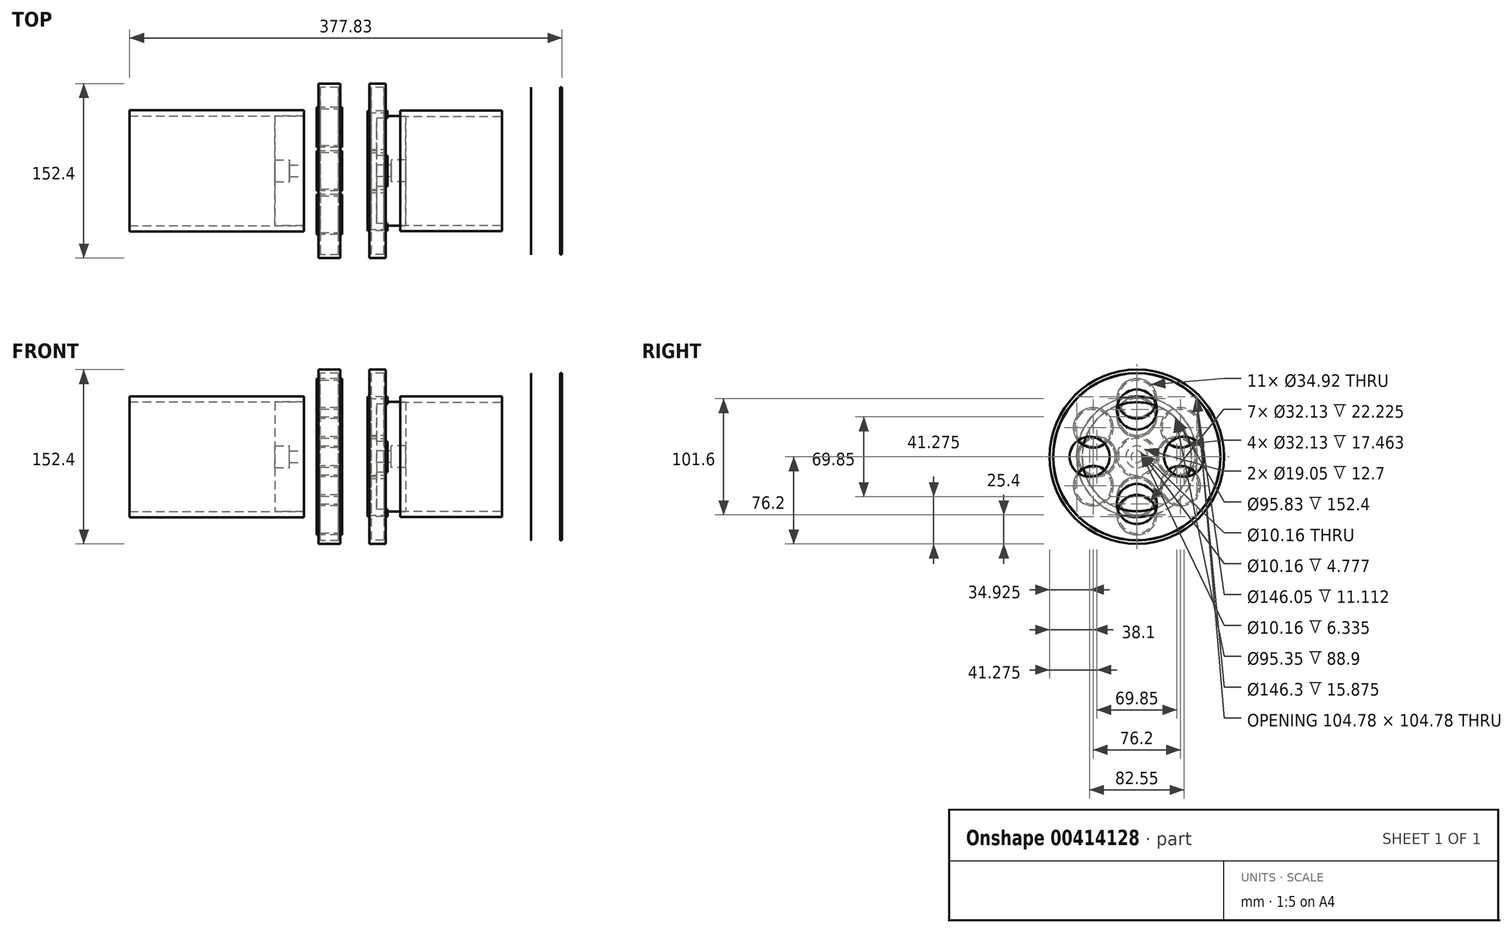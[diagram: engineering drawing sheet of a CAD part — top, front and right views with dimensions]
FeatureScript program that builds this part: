
annotation { "Feature Type Name" : "Feature", "Feature Type Description" : "" }
export const myFeature = defineFeature(function(context is Context, id is Id, definition is map)
    precondition{}
    {
        {
            var Q0;
            Q0=qCreatedBy(makeId("Front.planeOp"),FACE);
            var sketch = newSketch(context, id + "F0", { "sketchPlane" : qUnion([Q0])});
            skLineSegment(sketch, "E0", {"start": v(-64.69, 0) * mm, "end": v(54.13, 0) * mm, "construction": true});
            skLineSegment(sketch, "E1", {"start": v(25.4, 47.92) * mm, "end": v(50.8, 47.92) * mm});
            skLineSegment(sketch, "E2", {"start": v(50.8, 47.92) * mm, "end": v(50.8, 0) * mm});
            skLineSegment(sketch, "E3.trimOffspring", {"start": v(25.4, 0) * mm, "end": v(25.4, 47.92) * mm});
            skLineSegment(sketch, "E4", {"start": v(25.4, 0) * mm, "end": v(50.8, 0) * mm});
            skSolve(sketch);
        }
        {
            var Q0;
            Q0 = qSketchRegion(id + "F0", true);
            var Q1;
            Q1=sQuery(id+"F0.wireOp",EDGE,"E0");
            revolve(context, id + "F1", {"entities" : qUnion([Q0]), "axis" : qUnion([Q1]), "revolveType" : RevolveType.FULL});
        }
        {
            var Q0;
            Q0=makeQuery(id+"F1.opRevolve","SWEPT_FACE",FACE,{"disambiguationData":[OSD([sQuery(id+"F0.wireOp",EDGE,"E2")])]});
            var sketch = newSketch(context, id + "F2", { "sketchPlane" : qUnion([Q0])});
            skCircle(sketch, "E5.0", {"center": v(0, 0) * mm, "radius": 47.92 * mm});
            skCircle(sketch, "E6", {"center": v(0, 0) * mm, "radius": 52.92 * mm});
            skSolve(sketch);
        }
        {
            var Q0;
            Q0 = qSketchRegion(id + "F2", true);
            extrude(context, id + "F3", {"entities" : qUnion([Q0]), "oppositeDirection" : true, "depth" : 152.4 * mm});
        }
        {
            var Q0;
            Q0=makeQuery(id+"F1.opRevolve","SWEPT_FACE",FACE,{"disambiguationData":[OSD([sQuery(id+"F0.wireOp",EDGE,"E2")])]});
            cPlane(context, id + "F4", {"entities" : qUnion([Q0]), "cplaneType" : CPlaneType.OFFSET, "offset" : 12.7 * mm, "width" : 152.4 * mm, "height" : 152.4 * mm});
        }
        {
            var Q0;
            Q0=qCreatedBy(id+"F4.planeOp",FACE);
            var sketch = newSketch(context, id + "F5", { "sketchPlane" : qUnion([Q0])});
            skCircle(sketch, "E7", {"center": v(0, 0) * mm, "radius": 76.2 * mm});
            skLineSegment(sketch, "E8", {"start": v(0, 82.99) * mm, "end": v(0, -50.75) * mm, "construction": true});
            skPoint(sketch, "E8.startSnap0", {"position": v(0, 33.34) * mm});
            skLineSegment(sketch, "E9", {"start": v(-24.05, 0) * mm, "end": v(20.8, 0) * mm, "construction": true});
            skCircle(sketch, "E10", {"center": v(0, 0) * mm, "radius": 17.46 * mm});
            skCircle(sketch, "E11", {"center": v(0, 50.8) * mm, "radius": 17.46 * mm});
            skCircle(sketch, "E12", {"center": v(-38.1, 25.4) * mm, "radius": 17.46 * mm});
            skCircle(sketch, "E13", {"center": v(38.1, 25.4) * mm, "radius": 17.46 * mm});
            skCircle(sketch, "E14.MirrorC", {"center": v(-38.1, -25.4) * mm, "radius": 17.46 * mm});
            skCircle(sketch, "E15.MirrorC", {"center": v(0, -50.8) * mm, "radius": 17.46 * mm});
            skCircle(sketch, "E16.MirrorC", {"center": v(38.1, -25.4) * mm, "radius": 17.46 * mm});
            skSolve(sketch);
        }
        {
            var Q0;
            Q0=makeQuery(id+"F3.opExtrude","CAP_EDGE",EDGE,{"disambiguationData":[OSD([sQuery(id+"F2.wireOp",EDGE,"E6")])],"isStart":true});
            var Q1;
            Q1=sQuery(id+"F5.wireOp",EDGE,"E7");
            loft(context, id + "F6", {"bodyType" : ExtendedToolBodyType.SURFACE, "wireProfilesArray" : [{ "wireProfileEntities" : qUnion([Q0]) }, { "wireProfileEntities" : qUnion([Q1]) }]});
        }
        {
            var Q0;
            Q0=makeQuery(id+"F5.imprint","IMPRINT",FACE,{"disambiguationData":[TD([[makeQuery(id+"F5.imprint","IMPRINT",EDGE,{"derivedFrom":sQuery(id+"F5.wireOp",EDGE,"E7")}),1.0]])]});
            var Q1;
            {var subQ5=sQuery(id+"F5.wireOp",EDGE,"TezqSvzX-SYTh-v60S-WwQ1-Fqk2jw6tep4b");var subQ7=sQuery(id+"F5.wireOp",EDGE,"8UiiZq6U-XtdV-I6FB-cqel-CNXnzfDgyKXF.bottom");var subQ15=makeQuery(id+"F5.imprint","INTERSECT",VERTEX,{"derivedFrom":[subQ5,subQ7]});Q1=makeQuery(id+"F5.imprint","IMPRINT",FACE,{"disambiguationData":[TD([[makeQuery(id+"F5.imprint","IMPRINT",EDGE,{"disambiguationData":[TD([[subQ15,1.0]])],"derivedFrom":subQ5}),-1.0]])]});}
            extrude(context, id + "F7", {"entities" : qUnion([Q0, Q1]), "depth" : 1.59 * mm});
        }
        {
            var Q0;
            Q0=makeQuery(id+"F7.opExtrude","CAP_FACE",FACE,{"disambiguationData":[OSD([sQuery(id+"F5.wireOp",EDGE,"E7"),sQuery(id+"F5.wireOp",EDGE,"TezqSvzX-SYTh-v60S-WwQ1-Fqk2jw6tep4b"),sQuery(id+"F5.wireOp",EDGE,"lQJayD6f-2S0i-9Ahl-4Z4H-LnBthTz2M93B"),sQuery(id+"F5.wireOp",EDGE,"62HEBZpw-P9yn-nqEV-ZTk4-8jesArAcqBT5"),sQuery(id+"F5.wireOp",EDGE,"i2tJHl8b-q1yQ-QXrp-ARdM-XuqOJHXx20dm")])],"isStart":false});
            var sketch = newSketch(context, id + "F8", { "sketchPlane" : qUnion([Q0])});
            skCircle(sketch, "E17.0", {"center": v(0, 0) * mm, "radius": 76.2 * mm});
            skCircle(sketch, "E18", {"center": v(0, 0) * mm, "radius": 73.15 * mm});
            skSolve(sketch);
        }
        {
            var Q0;
            Q0 = qSketchRegion(id + "F8", true);
            extrude(context, id + "F9", {"entities" : qUnion([Q0]), "operationType" : NewBodyOperationType.ADD, "depth" : 17.46 * mm});
        }
        {
            var Q0;
            Q0=makeQuery(id+"F9.opExtrude","CAP_FACE",FACE,{"disambiguationData":[OSD([sQuery(id+"F8.wireOp",EDGE,"E17.0"),sQuery(id+"F8.wireOp",EDGE,"E18")])],"isStart":false});
            var sketch = newSketch(context, id + "F10", { "sketchPlane" : qUnion([Q0])});
            skCircle(sketch, "E19.0", {"center": v(0, 0) * mm, "radius": 73.15 * mm});
            skCircle(sketch, "E20.0", {"center": v(0, 0) * mm, "radius": 17.46 * mm});
            skCircle(sketch, "E21.0", {"center": v(-38.1, 25.4) * mm, "radius": 17.46 * mm});
            skCircle(sketch, "E21.1", {"center": v(0, 50.8) * mm, "radius": 17.46 * mm});
            skCircle(sketch, "E21.2", {"center": v(38.1, 25.4) * mm, "radius": 17.46 * mm});
            skCircle(sketch, "E21.3", {"center": v(38.1, -25.4) * mm, "radius": 17.46 * mm});
            skCircle(sketch, "E21.4", {"center": v(-38.1, -25.4) * mm, "radius": 17.46 * mm});
            skCircle(sketch, "E21.5", {"center": v(0, -50.8) * mm, "radius": 17.46 * mm});
            skSolve(sketch);
        }
        {
            var Q0;
            Q0 = qSketchRegion(id + "F10", true);
            extrude(context, id + "F11", {"entities" : qUnion([Q0]), "operationType" : NewBodyOperationType.ADD, "oppositeDirection" : true, "depth" : 1.59 * mm});
        }
        {
            var Q0;
            Q0=makeQuery(id+"F11.boolean.opBoolean","MERGE",FACE,{"derivedFrom":[makeQuery(id+"F9.opExtrude","CAP_FACE",FACE,{"disambiguationData":[OSD([sQuery(id+"F8.wireOp",EDGE,"E17.0"),sQuery(id+"F8.wireOp",EDGE,"E18")])],"isStart":false}),makeQuery(id+"F11.opExtrude","CAP_FACE",FACE,{"disambiguationData":[OSD([sQuery(id+"F10.wireOp",EDGE,"E19.0"),sQuery(id+"F10.wireOp",EDGE,"688862fc-af98-4b55-a261-9dea444bc1e7.0"),sQuery(id+"F10.wireOp",EDGE,"688862fc-af98-4b55-a261-9dea444bc1e7.1"),sQuery(id+"F10.wireOp",EDGE,"688862fc-af98-4b55-a261-9dea444bc1e7.2"),sQuery(id+"F10.wireOp",EDGE,"688862fc-af98-4b55-a261-9dea444bc1e7.3"),sQuery(id+"F10.wireOp",EDGE,"E20.0")])],"isStart":true})]});
            var sketch = newSketch(context, id + "F12", { "sketchPlane" : qUnion([Q0])});
            skCircle(sketch, "E22.0", {"center": v(0, 0) * mm, "radius": 17.46 * mm});
            skCircle(sketch, "E23", {"center": v(-38.1, 25.4) * mm, "radius": 16.07 * mm});
            skCircle(sketch, "E24", {"center": v(0, 0) * mm, "radius": 16.07 * mm});
            skCircle(sketch, "E25", {"center": v(0, 50.8) * mm, "radius": 16.07 * mm});
            skCircle(sketch, "E26.0", {"center": v(-38.1, 25.4) * mm, "radius": 17.46 * mm});
            skCircle(sketch, "E26.1", {"center": v(0, 50.8) * mm, "radius": 17.46 * mm});
            skCircle(sketch, "E26.2", {"center": v(38.1, 25.4) * mm, "radius": 17.46 * mm});
            skCircle(sketch, "E26.3", {"center": v(38.1, -25.4) * mm, "radius": 17.46 * mm});
            skCircle(sketch, "E26.4", {"center": v(0, -50.8) * mm, "radius": 17.46 * mm});
            skCircle(sketch, "E26.5", {"center": v(-38.1, -25.4) * mm, "radius": 17.46 * mm});
            skCircle(sketch, "E27", {"center": v(-38.1, -25.4) * mm, "radius": 16.07 * mm});
            skCircle(sketch, "E28", {"center": v(0, -50.8) * mm, "radius": 16.07 * mm});
            skCircle(sketch, "E29", {"center": v(38.1, -25.4) * mm, "radius": 16.07 * mm});
            skCircle(sketch, "E30", {"center": v(38.1, 25.4) * mm, "radius": 16.07 * mm});
            skSolve(sketch);
        }
        {
            var Q0;
            Q0 = qSketchRegion(id + "F12", true);
            extrude(context, id + "F13", {"entities" : qUnion([Q0]), "operationType" : NewBodyOperationType.ADD, "depth" : 1.59 * mm, "hasSecondDirection" : true, "secondDirectionOppositeDirection" : true, "secondDirectionDepth" : 20.64 * mm});
        }
        {
            var Q0;
            Q0=makeQuery(id+"F1.opRevolve","SWEPT_FACE",FACE,{"disambiguationData":[OSD([sQuery(id+"F0.wireOp",EDGE,"E3.trimOffspring")])]});
            var sketch = newSketch(context, id + "F14", { "sketchPlane" : qUnion([Q0])});
            skPoint(sketch, "E31", {"position": v(0, 0) * mm});
            skSolve(sketch);
        }
        {
            var Q0;
            Q0=sQuery(id+"F14.wireOp",VERTEX,"E31");
            var Q1;
            Q1=makeQuery(id+"F1.opRevolve","SWEPT_BODY",BODY,{"disambiguationData":[OSD([sQuery(id+"F0.wireOp",EDGE,"E1"),sQuery(id+"F0.wireOp",EDGE,"E2"),sQuery(id+"F0.wireOp",EDGE,"E3.trimOffspring"),sQuery(id+"F0.wireOp",EDGE,"E4")])]});
            hole(context, id + "F15", {"style" : HoleStyle.C_BORE, "endStyle" : HoleEndStyle.THROUGH, "holeDiameter" : 10.16 * mm, "cBoreDiameter" : 19.05 * mm, "cBoreDepth" : 12.7 * mm, "isTappedThrough" : true, "tappedDepth" : 12.7 * mm, "tapClearance" : 3, "locations" : qUnion([Q0]), "scope" : qUnion([Q1]), "startStyle" : HoleStartStyle.PART});
        }
        {
            var Q0;
            Q0=makeQuery(id+"F11.boolean.opBoolean","MERGE",FACE,{"derivedFrom":[makeQuery(id+"F9.opExtrude","CAP_FACE",FACE,{"disambiguationData":[OSD([sQuery(id+"F8.wireOp",EDGE,"E17.0"),sQuery(id+"F8.wireOp",EDGE,"E18")])],"isStart":false}),makeQuery(id+"F11.opExtrude","CAP_FACE",FACE,{"disambiguationData":[OSD([sQuery(id+"F10.wireOp",EDGE,"E19.0"),sQuery(id+"F10.wireOp",EDGE,"688862fc-af98-4b55-a261-9dea444bc1e7.0"),sQuery(id+"F10.wireOp",EDGE,"E20.0"),sQuery(id+"F10.wireOp",EDGE,"38044c42-0bda-4c24-9e16-b2cf3865c2e5.0"),sQuery(id+"F10.wireOp",EDGE,"38044c42-0bda-4c24-9e16-b2cf3865c2e5.1"),sQuery(id+"F10.wireOp",EDGE,"38044c42-0bda-4c24-9e16-b2cf3865c2e5.2"),sQuery(id+"F10.wireOp",EDGE,"38044c42-0bda-4c24-9e16-b2cf3865c2e5.3")])],"isStart":true})]});
            cPlane(context, id + "F16", {"entities" : qUnion([Q0]), "cplaneType" : CPlaneType.OFFSET, "offset" : 0.38 / 50.8 * mm, "width" : 152.4 * mm, "height" : 152.4 * mm});
        }
        {
            var Q0;
            Q0=makeQuery(id+"F6.opLoft","SWEPT_BODY",BODY,{"disambiguationData":[OSD([sQuery(id+"F2.wireOp",EDGE,"E6"),sQuery(id+"F5.wireOp",EDGE,"E7")])]});
            var Q1;
            Q1=makeQuery(id+"F1.opRevolve","SWEPT_BODY",BODY,{"disambiguationData":[OSD([sQuery(id+"F0.wireOp",EDGE,"E1"),sQuery(id+"F0.wireOp",EDGE,"E2"),sQuery(id+"F0.wireOp",EDGE,"7OPXWdJn-CDmA-Pngj-WDx1-qVM9FC09NOPd"),sQuery(id+"F0.wireOp",EDGE,"g0mtmRdn-CkNj-VwcP-hl4j-8XaxVRBAAcs2"),sQuery(id+"F0.wireOp",EDGE,"wG1DruvX-F1o3-LSDn-r3vX-2a799C9GLC4u"),sQuery(id+"F0.wireOp",EDGE,"jPwcn6bF-IbMm-58uC-mqah-eV2g20HCQfEf"),sQuery(id+"F0.wireOp",EDGE,"t1iSLtYn-DT6b-T7c2-KFmK-r26NDrkw72ja"),sQuery(id+"F0.wireOp",EDGE,"E3.trimOffspring")])]});
            var Q2;
            Q2=qCreatedBy(id+"F16.planeOp",FACE);
            mirror(context, id + "F17", {"entities" : qUnion([Q0, Q1]), "mirrorPlane" : qUnion([Q2])});
        }
        {
            var Q0;
            Q0=qCreatedBy(makeId("Front.planeOp"),FACE);
            var sketch = newSketch(context, id + "F18", { "sketchPlane" : qUnion([Q0])});
            skLineSegment(sketch, "E32", {"start": v(0, 0) * mm, "end": v(394.2, 0) * mm, "construction": true});
            skLineSegment(sketch, "E33", {"start": v(107.95, 0) * mm, "end": v(107.95, 76.2) * mm});
            skLineSegment(sketch, "E34", {"start": v(107.95, 76.2) * mm, "end": v(122.24, 76.2) * mm});
            skLineSegment(sketch, "E35", {"start": v(122.24, 76.2) * mm, "end": v(122.24, 0) * mm});
            skLineSegment(sketch, "E36", {"start": v(109.54, 0) * mm, "end": v(109.54, 73.03) * mm});
            skLineSegment(sketch, "E37", {"start": v(109.54, 73.03) * mm, "end": v(120.65, 73.03) * mm});
            skLineSegment(sketch, "E38", {"start": v(120.65, 73.03) * mm, "end": v(120.65, 0) * mm});
            skLineSegment(sketch, "E39", {"start": v(107.95, 0) * mm, "end": v(109.54, 0) * mm});
            skLineSegment(sketch, "E40", {"start": v(120.65, 0) * mm, "end": v(122.24, 0) * mm});
            skSolve(sketch);
        }
        {
            var Q0;
            Q0 = qSketchRegion(id + "F18", true);
            var Q1;
            Q1=sQuery(id+"F18.wireOp",EDGE,"E32");
            revolve(context, id + "F19", {"entities" : qUnion([Q0]), "axis" : qUnion([Q1]), "revolveType" : RevolveType.FULL});
        }
        {
            var Q0;
            Q0=makeQuery(id+"F19.opRevolve","SWEPT_FACE",FACE,{"disambiguationData":[OSD([sQuery(id+"F18.wireOp",EDGE,"E35")])]});
            var sketch = newSketch(context, id + "F20", { "sketchPlane" : qUnion([Q0])});
            skCircle(sketch, "E41", {"center": v(-34.93, 0) * mm, "radius": 17.46 * mm});
            skCircle(sketch, "E42", {"center": v(34.93, 0) * mm, "radius": 17.46 * mm});
            skCircle(sketch, "E43", {"center": v(0, 34.93) * mm, "radius": 17.46 * mm});
            skCircle(sketch, "E44", {"center": v(0, -34.93) * mm, "radius": 17.46 * mm});
            skCircle(sketch, "E45", {"center": v(0, 34.93) * mm, "radius": 16.07 * mm});
            skCircle(sketch, "E46", {"center": v(34.93, 0) * mm, "radius": 16.07 * mm});
            skCircle(sketch, "E47", {"center": v(0, -34.93) * mm, "radius": 16.07 * mm});
            skCircle(sketch, "E48", {"center": v(-34.93, 0) * mm, "radius": 16.07 * mm});
            skSolve(sketch);
        }
        {
            var Q0;
            Q0=makeQuery(id+"F20.imprint","IMPRINT",FACE,{"disambiguationData":[TD([[makeQuery(id+"F20.imprint","IMPRINT",EDGE,{"derivedFrom":sQuery(id+"F20.wireOp",EDGE,"E45")}),1.0]])]});
            var Q1;
            Q1=makeQuery(id+"F20.imprint","IMPRINT",FACE,{"disambiguationData":[TD([[makeQuery(id+"F20.imprint","IMPRINT",EDGE,{"derivedFrom":sQuery(id+"F20.wireOp",EDGE,"E48")}),1.0]])]});
            var Q2;
            Q2=makeQuery(id+"F20.imprint","IMPRINT",FACE,{"disambiguationData":[TD([[makeQuery(id+"F20.imprint","IMPRINT",EDGE,{"derivedFrom":sQuery(id+"F20.wireOp",EDGE,"E47")}),1.0]])]});
            var Q3;
            Q3=makeQuery(id+"F20.imprint","IMPRINT",FACE,{"disambiguationData":[TD([[makeQuery(id+"F20.imprint","IMPRINT",EDGE,{"derivedFrom":sQuery(id+"F20.wireOp",EDGE,"E46")}),1.0]])]});
            var Q4;
            Q4=makeQuery(id+"F19.opRevolve","SWEPT_FACE",FACE,{"disambiguationData":[OSD([sQuery(id+"F18.wireOp",EDGE,"E33")])]});
            extrude(context, id + "F21", {"entities" : qUnion([Q0, Q1, Q2, Q3]), "operationType" : NewBodyOperationType.REMOVE, "endBound" : BoundingType.UP_TO_SURFACE, "oppositeDirection" : true, "endBoundEntityFace" : qUnion([Q4]), "depth" : 25.4 * mm});
        }
        {
            var Q0;
            Q0=makeQuery(id+"F20.imprint","IMPRINT",FACE,{"disambiguationData":[TD([[makeQuery(id+"F20.imprint","IMPRINT",EDGE,{"derivedFrom":sQuery(id+"F20.wireOp",EDGE,"E43")}),1.0]])]});
            var Q1;
            Q1=makeQuery(id+"F20.imprint","IMPRINT",FACE,{"disambiguationData":[TD([[makeQuery(id+"F20.imprint","IMPRINT",EDGE,{"derivedFrom":sQuery(id+"F20.wireOp",EDGE,"E42")}),1.0]])]});
            var Q2;
            Q2=makeQuery(id+"F20.imprint","IMPRINT",FACE,{"disambiguationData":[TD([[makeQuery(id+"F20.imprint","IMPRINT",EDGE,{"derivedFrom":sQuery(id+"F20.wireOp",EDGE,"E44")}),1.0]])]});
            var Q3;
            Q3=makeQuery(id+"F20.imprint","IMPRINT",FACE,{"disambiguationData":[TD([[makeQuery(id+"F20.imprint","IMPRINT",EDGE,{"derivedFrom":sQuery(id+"F20.wireOp",EDGE,"E41")}),1.0]])]});
            extrude(context, id + "F22", {"entities" : qUnion([Q0, Q1, Q2, Q3]), "operationType" : NewBodyOperationType.ADD, "depth" : 1.59 * mm, "hasSecondDirection" : true, "secondDirectionOppositeDirection" : true, "secondDirectionDepth" : 15.88 * mm});
        }
        {
            var Q0;
            Q0=qCreatedBy(makeId("Front.planeOp"),FACE);
            var sketch = newSketch(context, id + "F23", { "sketchPlane" : qUnion([Q0])});
            skLineSegment(sketch, "E49", {"start": v(133.19, 0) * mm, "end": v(56.92, 0) * mm, "construction": true});
            skLineSegment(sketch, "E50.bottom", {"start": v(134.94, 52.65) * mm, "end": v(223.84, 52.65) * mm});
            skLineSegment(sketch, "E50.top", {"start": v(134.94, 47.68) * mm, "end": v(223.84, 47.68) * mm});
            skLineSegment(sketch, "E50.left", {"start": v(134.94, 52.65) * mm, "end": v(134.94, 47.68) * mm});
            skLineSegment(sketch, "E50.right", {"start": v(223.84, 52.65) * mm, "end": v(223.84, 47.68) * mm});
            skSolve(sketch);
        }
        {
            var Q0;
            Q0=makeQuery(id+"F23.imprint","IMPRINT",FACE,{"disambiguationData":[TD([[makeQuery(id+"F23.imprint","IMPRINT",EDGE,{"derivedFrom":sQuery(id+"F23.wireOp",EDGE,"E50.bottom")}),-1.0]])]});
            var Q1;
            Q1=sQuery(id+"F23.wireOp",EDGE,"E49");
            revolve(context, id + "F24", {"entities" : qUnion([Q0]), "axis" : qUnion([Q1]), "revolveType" : RevolveType.FULL});
        }
        {
            var Q0;
            Q0=makeQuery(id+"F24.opRevolve","SWEPT_FACE",FACE,{"disambiguationData":[OSD([sQuery(id+"F23.wireOp",EDGE,"E50.right")])]});
            cPlane(context, id + "F25", {"entities" : qUnion([Q0]), "cplaneType" : CPlaneType.OFFSET, "offset" : 25.4 * mm, "width" : 152.4 * mm, "height" : 152.4 * mm});
        }
        {
            var Q0;
            Q0=qCreatedBy(id+"F25.planeOp",FACE);
            var sketch = newSketch(context, id + "F26", { "sketchPlane" : qUnion([Q0])});
            skCircle(sketch, "E51.0", {"center": v(0, 50.8) * mm, "radius": 17.46 * mm});
            skCircle(sketch, "E51.1", {"center": v(38.1, 25.4) * mm, "radius": 17.46 * mm});
            skCircle(sketch, "E51.2", {"center": v(-38.1, 25.4) * mm, "radius": 17.46 * mm});
            skCircle(sketch, "E51.3", {"center": v(0, 0) * mm, "radius": 17.46 * mm});
            skCircle(sketch, "E51.4", {"center": v(-38.1, -25.4) * mm, "radius": 17.46 * mm});
            skCircle(sketch, "E51.5", {"center": v(0, -50.8) * mm, "radius": 17.46 * mm});
            skCircle(sketch, "E51.6", {"center": v(38.1, -25.4) * mm, "radius": 17.46 * mm});
            skCircle(sketch, "E52.0", {"center": v(0, 0) * mm, "radius": 73.15 * mm});
            skSolve(sketch);
        }
        {
            var Q0;
            Q0 = qSketchRegion(id + "F26", true);
            extrude(context, id + "F27", {"entities" : qUnion([Q0]), "depth" : 1 / 406.4 * mm});
        }
        {
            var Q0;
            Q0=qCreatedBy(id+"F25.planeOp",FACE);
            cPlane(context, id + "F28", {"entities" : qUnion([Q0]), "cplaneType" : CPlaneType.OFFSET, "offset" : 25.4 * mm, "width" : 152.4 * mm, "height" : 152.4 * mm});
        }
        {
            var Q0;
            Q0=qCreatedBy(id+"F28.planeOp",FACE);
            var sketch = newSketch(context, id + "F29", { "sketchPlane" : qUnion([Q0])});
            skCircle(sketch, "E53.0", {"center": v(0, 41.28) * mm, "radius": 17.46 * mm});
            skCircle(sketch, "E53.1", {"center": v(41.28, 0) * mm, "radius": 17.46 * mm});
            skCircle(sketch, "E53.2", {"center": v(0, -41.28) * mm, "radius": 17.46 * mm});
            skCircle(sketch, "E53.3", {"center": v(-41.28, 0) * mm, "radius": 17.46 * mm});
            skCircle(sketch, "E54.0", {"center": v(0, 0) * mm, "radius": 73.03 * mm});
            skCircle(sketch, "E55", {"center": v(0, 0) * mm, "radius": 41.28 * mm, "construction": true});
            skSolve(sketch);
        }
        {
            var Q0;
            Q0 = qSketchRegion(id + "F29", true);
            extrude(context, id + "F30", {"entities" : qUnion([Q0]), "depth" : 1.59 * mm});
        }
    });
